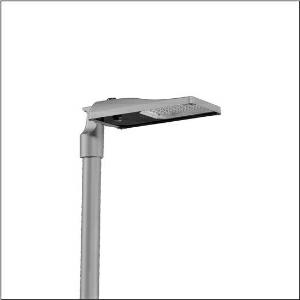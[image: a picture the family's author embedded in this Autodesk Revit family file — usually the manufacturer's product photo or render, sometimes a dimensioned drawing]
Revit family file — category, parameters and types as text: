
# Revit family: streetlight_sl_31_mini___p0_8a_5xh6u31t08ha_cf92
name_source: partatom
category: Lighting Fixtures
units: mm (PartAtom-declared; Revit-internal decimal feet)

## family parameters
Cut with Voids When Loaded = No
Host = Face
Light Source = No
Part Type = Normal
Room Calculation Point = No
Round Connector Dimension = Use Diameter
Shared = No

## types (1)
- --- (1 x LED, 9320 lm, 68.3 W, 3000K)
    Apparent Load = 68 VA
    CIE Flux Codes = 33 69 96 100 100
    Color Rendering = 70
    Color Temperature = 3000K
    Default Elevation = 1800 mm
    Description = Streetlight SL 31 mini D4i, Desk-Remote mast luminaire for post-top, side-entry; light control with lens of PMMA; light distribution: P0.8a, direct asymmetric distribution, for standard-compliant lighting for roads and squares; LED: luminous flux: 9.320lm, light colour: 730, colour temperature: 3000K; luminous efficacy: 136,5lm/W; control: pre-setting: logarithmic dimming characteristic, flexible luminous flux parameterisation, time-dependent luminous flux control, constant luminous flux control, power reduction, intelligent temperature release in ECG and LED module, overheat protection; luminaire housing, of diecast aluminium, SITECO metallic grey (DB 702S), corrosivity category C5 high according to DIN EN ISO 12944; cover of toughened safety glass, transparent, opened without tools; mast flange of diecast aluminium, SITECO metallic grey (DB 702S), spigot size: 76/60mm, mast flange included unmounted; cable length: 8,5m, connection cable pre-assembled; mains connection: 220..240V, AC, 50/60Hz; power consumption (at start of service life): 68,3W / (at end of service life): 74,5W / (with reduced operation 50%): 29,5W; protection rating (complete): IP66; insulation class (complete): insulation class II (safety insulation); impact resistance: IK09; certification: CE, ENEC, ENEC+, VDE, UKCA, ZD4i; permissible operating ambient temperature for outdoor applications: -40..+50°C; packaging unit: 1 piece

Light Distribution: P0.8a
    Height = 76 mm
    Lamp = 1 x LED
    Lamp Light Flux = 9320 lm
    Lamp Power = 68.3 W
    Lamp count = 1
    Length = 547 mm
    Luminous efficacy = 136 lm/W
    Manufacturer = Siteco
    ModVariant = No
    Model = 5XH6U31T08HA
    Number of Poles = 1
    OnlyDefault = Yes
    Power Factor = 1
    Product Name = Streetlight SL 31 mini | P0.8a
    Product group = mast luminaire | pylon top
    ProductGroupID = 6100
    Protection Class = Protection class II
    Protection Degree = IP 66
    RLX_Detail_Level = 1
    RLX_Emergency_Light_Flux = 0 lm
    RLX_Emergency_Type = 0
    RLX_Emergency_Type_DB = No
    RlxData = <blob elided: 24101 chars, md5=65d6dcd1>
    Socket = socket
    Standby Power = 0 W
    System Light Flux = 9320 lm
    System Power = 68 W
    Type Comments = factory setting: luminous flux: 100 % | dim-lin: 254 | 692 mA
    Type Image = l_1300332.jpg
    URL = http://relux.com
    VarID = @adj_027527
    Voltage = 0 V
    Weight = 0.00 kg
    Width = 265 mm

## geometry (parser evidence)
native form markers: Blend x4, Sweep x11
no freeform markers — native parametric forms only
